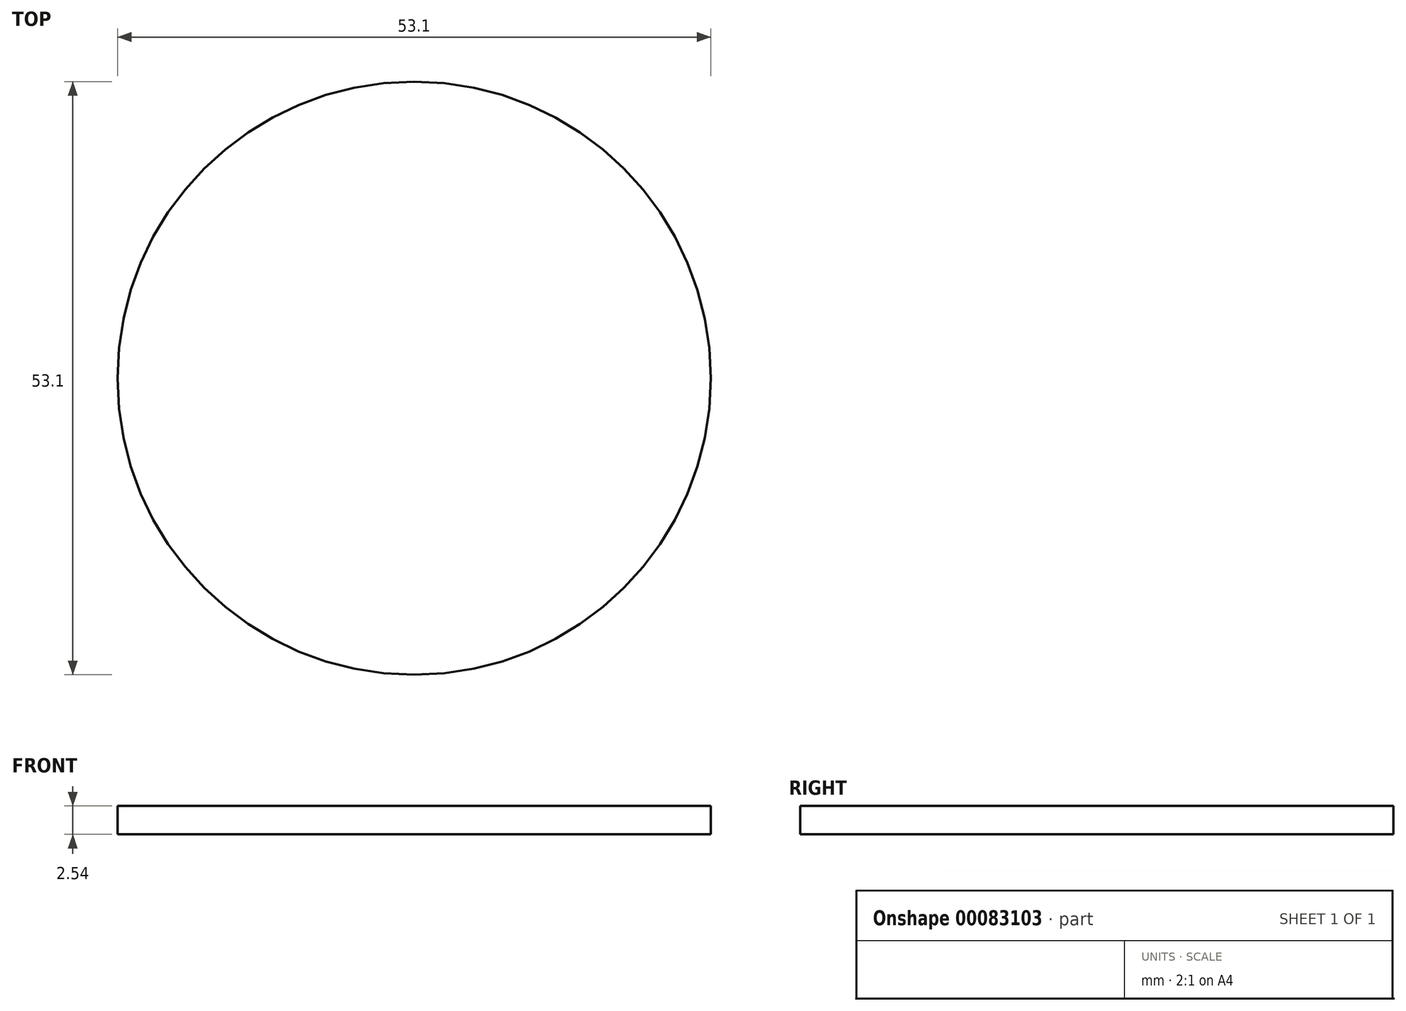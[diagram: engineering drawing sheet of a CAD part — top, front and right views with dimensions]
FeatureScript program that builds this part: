
annotation { "Feature Type Name" : "Feature", "Feature Type Description" : "" }
export const myFeature = defineFeature(function(context is Context, id is Id, definition is map)
    precondition{}
    {
        {
            var Q0;
            Q0=qCreatedBy(makeId("Top.planeOp"),FACE);
            var sketch = newSketch(context, id + "F0", { "sketchPlane" : qUnion([Q0])});
            skCircle(sketch, "E0", {"center": v(0, 0) * mm, "radius": 26.55 * mm});
            skSolve(sketch);
        }
        {
            var Q0;
            Q0=makeQuery(id+"F0.imprint","IMPRINT",FACE,{"disambiguationData":[TD([[makeQuery(id+"F0.imprint","IMPRINT",EDGE,{"derivedFrom":sQuery(id+"F0.wireOp",EDGE,"E0")}),1.0]])]});
            var Q1;
            Q1=sQuery(id+"F0.wireOp",EDGE,"E0");
            extrude(context, id + "F1", {"entities" : qUnion([Q0]), "surfaceEntities" : qUnion([Q1]), "depth" : 2.54 * mm});
        }
    });
